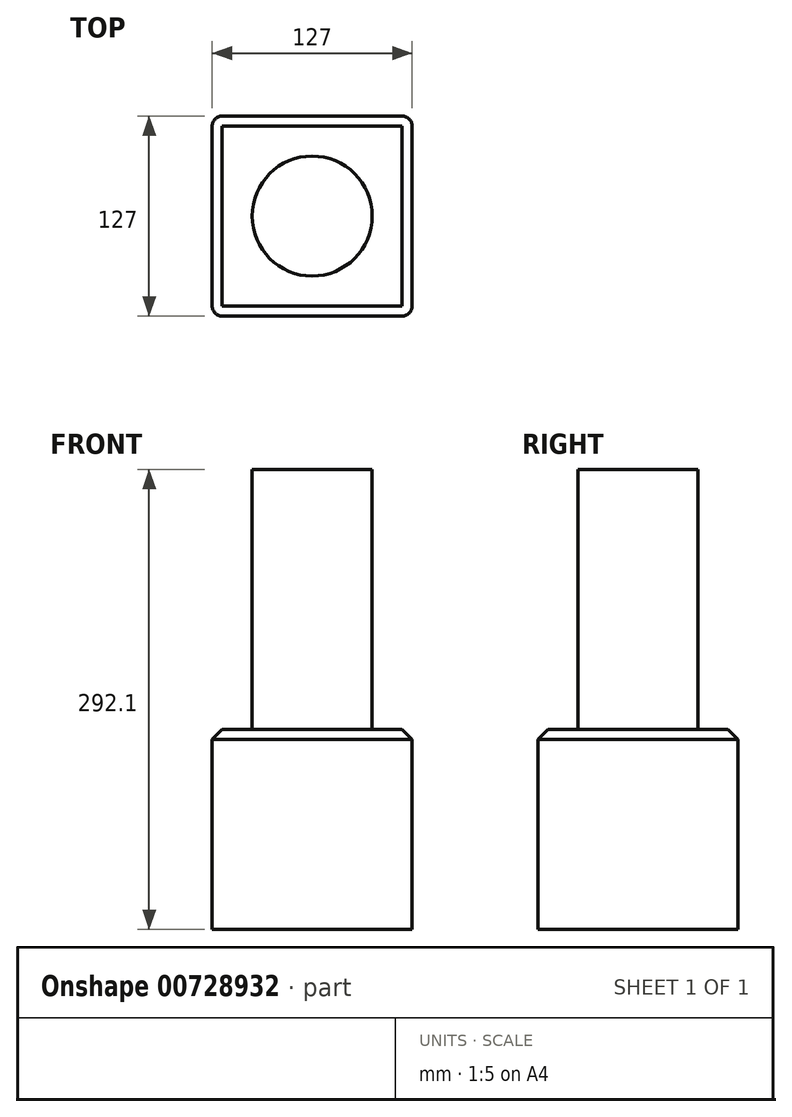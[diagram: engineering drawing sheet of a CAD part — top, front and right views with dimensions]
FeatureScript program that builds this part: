
annotation { "Feature Type Name" : "Feature", "Feature Type Description" : "" }
export const myFeature = defineFeature(function(context is Context, id is Id, definition is map)
    precondition{}
    {
        {
            var Q0;
            Q0=qCreatedBy(makeId("Top.planeOp"),FACE);
            var sketch = newSketch(context, id + "F0", { "sketchPlane" : qUnion([Q0])});
            skLineSegment(sketch, "E0.bottom", {"start": v(63.5, 63.5) * mm, "end": v(-63.5, 63.5) * mm});
            skLineSegment(sketch, "E0.top", {"start": v(63.5, -63.5) * mm, "end": v(-63.5, -63.5) * mm});
            skLineSegment(sketch, "E0.left", {"start": v(63.5, 63.5) * mm, "end": v(63.5, -63.5) * mm});
            skLineSegment(sketch, "E0.right", {"start": v(-63.5, 63.5) * mm, "end": v(-63.5, -63.5) * mm});
            skPoint(sketch, "E0.middle", {"position": v(0, 0) * mm});
            skCircle(sketch, "E1", {"center": v(0, 0) * mm, "radius": 38.1 * mm});
            skSolve(sketch);
        }
        {
            var Q0;
            Q0=makeQuery(id+"F0.imprint","IMPRINT",FACE,{"disambiguationData":[TD([[makeQuery(id+"F0.imprint","IMPRINT",EDGE,{"derivedFrom":sQuery(id+"F0.wireOp",EDGE,"E0.bottom")}),1.0]])]});
            var Q1;
            Q1=makeQuery(id+"F0.imprint","IMPRINT",FACE,{"disambiguationData":[TD([[makeQuery(id+"F0.imprint","IMPRINT",EDGE,{"derivedFrom":sQuery(id+"F0.wireOp",EDGE,"E1")}),1.0]])]});
            extrude(context, id + "F1", {"entities" : qUnion([Q0, Q1]), "oppositeDirection" : true, "depth" : 127 * mm, "offsetDistance" : 25.4 * mm});
        }
        {
            var Q0;
            Q0=makeQuery(id+"F0.imprint","IMPRINT",FACE,{"disambiguationData":[TD([[makeQuery(id+"F0.imprint","IMPRINT",EDGE,{"derivedFrom":sQuery(id+"F0.wireOp",EDGE,"E1")}),1.0]])]});
            extrude(context, id + "F2", {"entities" : qUnion([Q0]), "operationType" : NewBodyOperationType.ADD, "depth" : 165.1 * mm, "offsetDistance" : 25.4 * mm});
        }
        {
            var Q0;
            Q0=makeQuery(id+"F1.opExtrude","SWEPT_EDGE",EDGE,{"disambiguationData":[OSD([sQuery(id+"F0.wireOp",EDGE,"E0.top"),sQuery(id+"F0.wireOp",EDGE,"E0.right")])]});
            var Q1;
            Q1=makeQuery(id+"F1.opExtrude","SWEPT_EDGE",EDGE,{"disambiguationData":[OSD([sQuery(id+"F0.wireOp",EDGE,"E0.top"),sQuery(id+"F0.wireOp",EDGE,"E0.left")])]});
            var Q2;
            Q2=makeQuery(id+"F1.opExtrude","SWEPT_EDGE",EDGE,{"disambiguationData":[OSD([sQuery(id+"F0.wireOp",EDGE,"E0.bottom"),sQuery(id+"F0.wireOp",EDGE,"E0.left")])]});
            var Q3;
            Q3=makeQuery(id+"F1.opExtrude","SWEPT_EDGE",EDGE,{"disambiguationData":[OSD([sQuery(id+"F0.wireOp",EDGE,"E0.bottom"),sQuery(id+"F0.wireOp",EDGE,"E0.right")])]});
            fillet(context, id + "F3", {"entities" : qUnion([Q0, Q1, Q2, Q3]), "radius" : 6.35 * mm, "tangentPropagation" : true, "allowEdgeOverflow" : false});
        }
        {
            var Q0;
            Q0=makeQuery(id+"F1.opExtrude","CAP_EDGE",EDGE,{"disambiguationData":[OSD([sQuery(id+"F0.wireOp",EDGE,"E0.top")])],"isStart":true});
            chamfer(context, id + "F4", {"entities" : qUnion([Q0]), "width" : 6.35 * mm, "tangentPropagation" : true});
        }
    });
